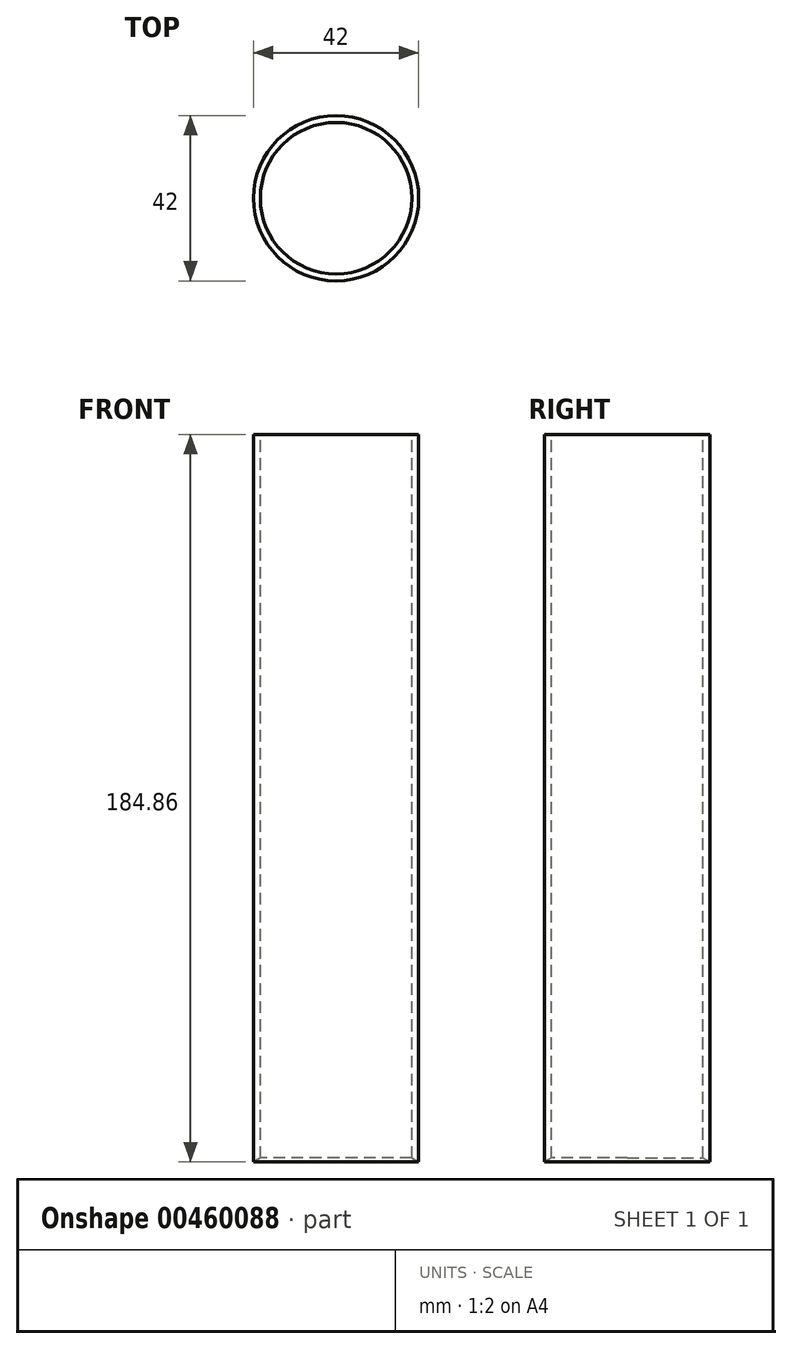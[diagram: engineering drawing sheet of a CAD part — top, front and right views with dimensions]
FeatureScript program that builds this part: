
annotation { "Feature Type Name" : "Feature", "Feature Type Description" : "" }
export const myFeature = defineFeature(function(context is Context, id is Id, definition is map)
    precondition{}
    {
        {
            var Q0;
            Q0=qCreatedBy(makeId("Front.planeOp"),FACE);
            var sketch = newSketch(context, id + "F0", { "sketchPlane" : qUnion([Q0])});
            skLineSegment(sketch, "E0.bottom", {"start": v(10.5, -92.5) * mm, "end": v(-10.5, -92.5) * mm});
            skLineSegment(sketch, "E0.top", {"start": v(10.5, 92.5) * mm, "end": v(-10.5, 92.5) * mm});
            skLineSegment(sketch, "E0.left", {"start": v(10.5, -92.5) * mm, "end": v(10.5, 92.5) * mm});
            skLineSegment(sketch, "E0.right", {"start": v(-10.5, -92.5) * mm, "end": v(-10.5, 92.5) * mm});
            skPoint(sketch, "E0.middle", {"position": v(0, 0) * mm});
            skSolve(sketch);
        }
        {
            var Q0;
            Q0 = qSketchRegion(id + "F0", true);
            var Q1;
            Q1=sQuery(id+"F0.wireOp",EDGE,"E0.right");
            revolve(context, id + "F1", {"entities" : qUnion([Q0]), "axis" : qUnion([Q1]), "revolveType" : RevolveType.FULL});
        }
        {
            var Q0;
            Q0=makeQuery(id+"F1.opRevolve","SWEPT_FACE",FACE,{"disambiguationData":[OSD([sQuery(id+"F0.wireOp",EDGE,"E0.top")])]});
            var sketch = newSketch(context, id + "F2", { "sketchPlane" : qUnion([Q0])});
            skCircle(sketch, "E1.0", {"center": v(-10.5, 0) * mm, "radius": 19.25 * mm});
            skSolve(sketch);
        }
        {
            var Q0;
            Q0=makeQuery(id+"F2.imprint","IMPRINT",FACE,{"disambiguationData":[TD([[makeQuery(id+"F2.imprint","IMPRINT",EDGE,{"derivedFrom":sQuery(id+"F2.wireOp",EDGE,"E1.0")}),1.0]])]});
            extrude(context, id + "F3", {"entities" : qUnion([Q0]), "operationType" : NewBodyOperationType.REMOVE, "endBound" : BoundingType.THROUGH_ALL, "oppositeDirection" : true, "depth" : 25 * mm});
        }
        {
            var Q0;
            Q0=makeQuery(id+"F3.boolean.opBoolean","COPY",EDGE,{"derivedFrom":makeQuery(id+"F3.opExtrude","CAP_EDGE",EDGE,{"disambiguationData":[OSD([sQuery(id+"F2.wireOp",EDGE,"E1.0")])],"isStart":true})});
            var Q1;
            Q1=makeQuery(id+"F3.boolean.opBoolean","INTERSECT",EDGE,{"derivedFrom":[makeQuery(id+"F1.opRevolve","SWEPT_FACE",FACE,{"disambiguationData":[OSD([sQuery(id+"F0.wireOp",EDGE,"E0.bottom")])]}),makeQuery(id+"F3.opExtrude","SWEPT_FACE",FACE,{"disambiguationData":[OSD([sQuery(id+"F2.wireOp",EDGE,"E1.0")])]})]});
            chamfer(context, id + "F4", {"entities" : qUnion([Q0, Q1]), "chamferType" : ChamferType.OFFSET_ANGLE, "width" : 2 * mm, "oppositeDirection" : false, "angle" : 30 * degree, "tangentPropagation" : true});
        }
    });
